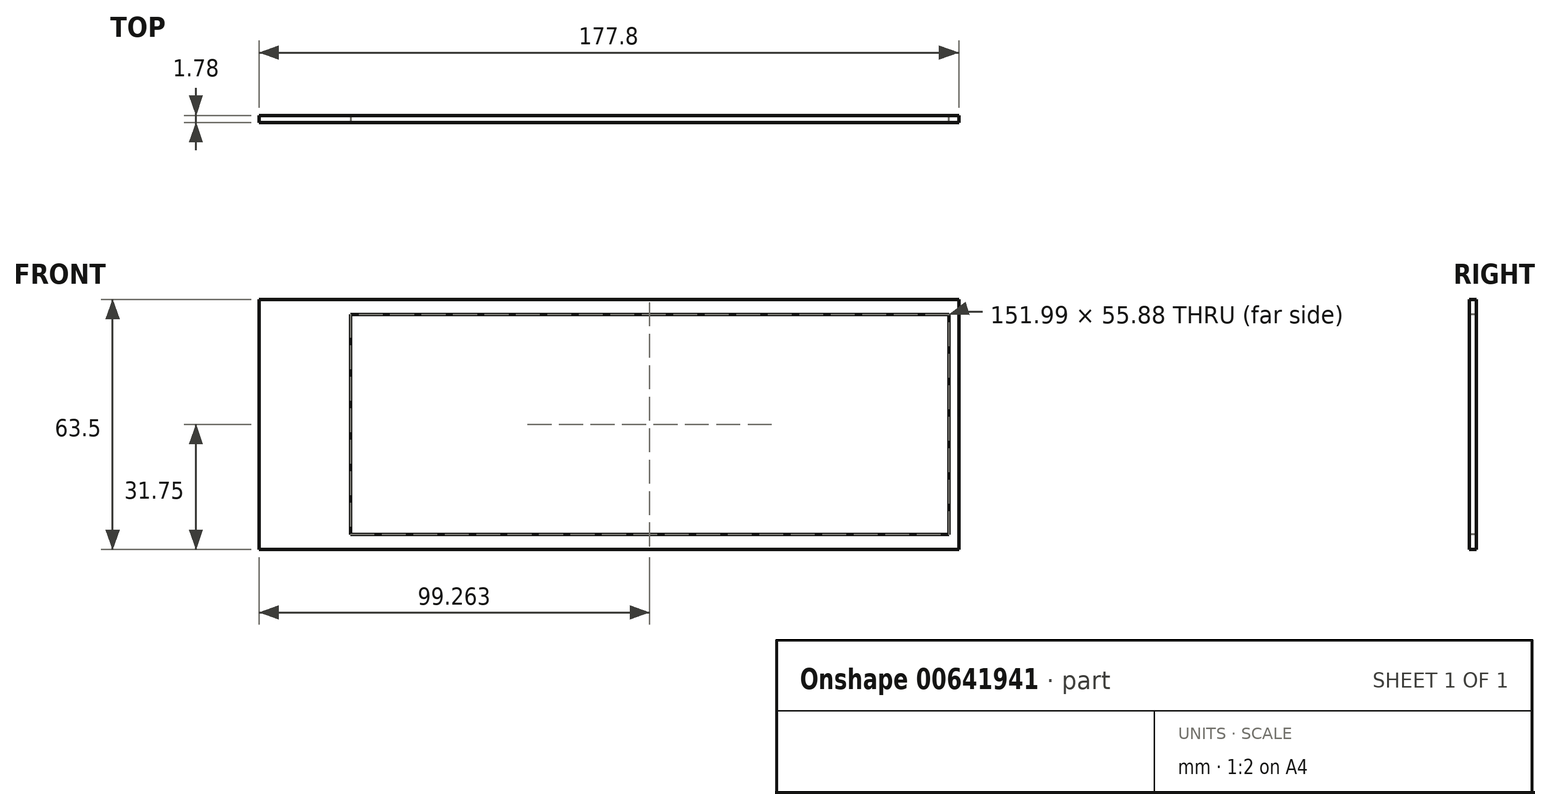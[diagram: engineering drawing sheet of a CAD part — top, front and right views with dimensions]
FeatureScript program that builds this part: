
annotation { "Feature Type Name" : "Feature", "Feature Type Description" : "" }
export const myFeature = defineFeature(function(context is Context, id is Id, definition is map)
    precondition{}
    {
        {
            var Q0;
            Q0=qCreatedBy(makeId("Front.planeOp"),FACE);
            var sketch = newSketch(context, id + "F0", { "sketchPlane" : qUnion([Q0])});
            skLineSegment(sketch, "E0.bottom", {"start": v(88.9, -31.75) * mm, "end": v(-88.9, -31.75) * mm});
            skLineSegment(sketch, "E0.top", {"start": v(88.9, 31.75) * mm, "end": v(-88.9, 31.75) * mm});
            skLineSegment(sketch, "E0.left", {"start": v(88.9, -31.75) * mm, "end": v(88.9, 31.75) * mm});
            skLineSegment(sketch, "E0.right", {"start": v(-88.9, -31.75) * mm, "end": v(-88.9, 31.75) * mm});
            skPoint(sketch, "E0.middle", {"position": v(0, 0) * mm});
            skLineSegment(sketch, "E1.bottom", {"start": v(86.36, -27.94) * mm, "end": v(-86.36, -27.94) * mm});
            skLineSegment(sketch, "E1.top", {"start": v(86.36, 27.94) * mm, "end": v(-86.36, 27.94) * mm});
            skLineSegment(sketch, "E1.left", {"start": v(86.36, -27.94) * mm, "end": v(86.36, 27.94) * mm});
            skLineSegment(sketch, "E1.right", {"start": v(-86.36, -27.94) * mm, "end": v(-86.36, 27.94) * mm});
            skLineSegment(sketch, "E2.bottom", {"start": v(-79.45, 27.94) * mm, "end": v(-72.54, 27.94) * mm});
            skLineSegment(sketch, "E2.top", {"start": v(-79.45, -27.94) * mm, "end": v(-72.54, -27.94) * mm});
            skLineSegment(sketch, "E2.left", {"start": v(-79.45, 27.94) * mm, "end": v(-79.45, -27.94) * mm});
            skLineSegment(sketch, "E2.right", {"start": v(-72.54, 27.94) * mm, "end": v(-72.54, -27.94) * mm});
            skLineSegment(sketch, "E3.1.0.0", {"start": v(-65.63, 27.94) * mm, "end": v(-58.72, 27.94) * mm});
            skLineSegment(sketch, "E3.1.0.1", {"start": v(-65.63, -27.94) * mm, "end": v(-58.72, -27.94) * mm});
            skLineSegment(sketch, "E3.1.0.2", {"start": v(-65.63, 27.94) * mm, "end": v(-65.63, -27.94) * mm});
            skLineSegment(sketch, "E3.1.0.3", {"start": v(-58.72, 27.94) * mm, "end": v(-58.72, -27.94) * mm});
            skLineSegment(sketch, "E3.2.0.0", {"start": v(-51.82, 27.94) * mm, "end": v(-44.9, 27.94) * mm});
            skLineSegment(sketch, "E3.2.0.1", {"start": v(-51.82, -27.94) * mm, "end": v(-44.9, -27.94) * mm});
            skLineSegment(sketch, "E3.2.0.2", {"start": v(-51.82, 27.94) * mm, "end": v(-51.82, -27.94) * mm});
            skLineSegment(sketch, "E3.2.0.3", {"start": v(-44.9, 27.94) * mm, "end": v(-44.9, -27.94) * mm});
            skLineSegment(sketch, "E3.direction1", {"start": v(-79.45, -27.94) * mm, "end": v(-65.63, -27.94) * mm, "construction": true});
            skLineSegment(sketch, "E4.0.3.0", {"start": v(-38, 27.94) * mm, "end": v(-31.09, 27.94) * mm});
            skLineSegment(sketch, "E4.3.3.0", {"start": v(-38, -27.94) * mm, "end": v(-31.09, -27.94) * mm});
            skLineSegment(sketch, "E4.6.3.0", {"start": v(-38, 27.94) * mm, "end": v(-38, -27.94) * mm});
            skLineSegment(sketch, "E4.9.3.0", {"start": v(-31.09, 27.94) * mm, "end": v(-31.09, -27.94) * mm});
            skLineSegment(sketch, "E4.0.4.0", {"start": v(-24.18, 27.94) * mm, "end": v(-17.27, 27.94) * mm});
            skLineSegment(sketch, "E4.3.4.0", {"start": v(-24.18, -27.94) * mm, "end": v(-17.27, -27.94) * mm});
            skLineSegment(sketch, "E4.6.4.0", {"start": v(-24.18, 27.94) * mm, "end": v(-24.18, -27.94) * mm});
            skLineSegment(sketch, "E4.9.4.0", {"start": v(-17.27, 27.94) * mm, "end": v(-17.27, -27.94) * mm});
            skLineSegment(sketch, "E4.0.5.0", {"start": v(-10.36, 27.94) * mm, "end": v(-3.45, 27.94) * mm});
            skLineSegment(sketch, "E4.3.5.0", {"start": v(-10.36, -27.94) * mm, "end": v(-3.45, -27.94) * mm});
            skLineSegment(sketch, "E4.6.5.0", {"start": v(-10.36, 27.94) * mm, "end": v(-10.36, -27.94) * mm});
            skLineSegment(sketch, "E4.9.5.0", {"start": v(-3.45, 27.94) * mm, "end": v(-3.45, -27.94) * mm});
            skLineSegment(sketch, "E4.0.6.0", {"start": v(3.45, 27.94) * mm, "end": v(10.36, 27.94) * mm});
            skLineSegment(sketch, "E4.3.6.0", {"start": v(3.45, -27.94) * mm, "end": v(10.36, -27.94) * mm});
            skLineSegment(sketch, "E4.6.6.0", {"start": v(3.45, 27.94) * mm, "end": v(3.45, -27.94) * mm});
            skLineSegment(sketch, "E4.9.6.0", {"start": v(10.36, 27.94) * mm, "end": v(10.36, -27.94) * mm});
            skLineSegment(sketch, "E4.0.7.0", {"start": v(17.27, 27.94) * mm, "end": v(24.18, 27.94) * mm});
            skLineSegment(sketch, "E4.3.7.0", {"start": v(17.27, -27.94) * mm, "end": v(24.18, -27.94) * mm});
            skLineSegment(sketch, "E4.6.7.0", {"start": v(17.27, 27.94) * mm, "end": v(17.27, -27.94) * mm});
            skLineSegment(sketch, "E4.9.7.0", {"start": v(24.18, 27.94) * mm, "end": v(24.18, -27.94) * mm});
            skLineSegment(sketch, "E4.0.8.0", {"start": v(31.09, 27.94) * mm, "end": v(38, 27.94) * mm});
            skLineSegment(sketch, "E4.3.8.0", {"start": v(31.09, -27.94) * mm, "end": v(38, -27.94) * mm});
            skLineSegment(sketch, "E4.6.8.0", {"start": v(31.09, 27.94) * mm, "end": v(31.09, -27.94) * mm});
            skLineSegment(sketch, "E4.9.8.0", {"start": v(38, 27.94) * mm, "end": v(38, -27.94) * mm});
            skLineSegment(sketch, "E4.0.9.0", {"start": v(44.9, 27.94) * mm, "end": v(51.82, 27.94) * mm});
            skLineSegment(sketch, "E4.3.9.0", {"start": v(44.9, -27.94) * mm, "end": v(51.82, -27.94) * mm});
            skLineSegment(sketch, "E4.6.9.0", {"start": v(44.9, 27.94) * mm, "end": v(44.9, -27.94) * mm});
            skLineSegment(sketch, "E4.9.9.0", {"start": v(51.82, 27.94) * mm, "end": v(51.82, -27.94) * mm});
            skLineSegment(sketch, "E4.0.10.0", {"start": v(58.72, 27.94) * mm, "end": v(65.63, 27.94) * mm});
            skLineSegment(sketch, "E4.3.10.0", {"start": v(58.72, -27.94) * mm, "end": v(65.63, -27.94) * mm});
            skLineSegment(sketch, "E4.6.10.0", {"start": v(58.72, 27.94) * mm, "end": v(58.72, -27.94) * mm});
            skLineSegment(sketch, "E4.9.10.0", {"start": v(65.63, 27.94) * mm, "end": v(65.63, -27.94) * mm});
            skLineSegment(sketch, "E4.0.11.0", {"start": v(72.54, 27.94) * mm, "end": v(79.45, 27.94) * mm});
            skLineSegment(sketch, "E4.3.11.0", {"start": v(72.54, -27.94) * mm, "end": v(79.45, -27.94) * mm});
            skLineSegment(sketch, "E4.6.11.0", {"start": v(72.54, 27.94) * mm, "end": v(72.54, -27.94) * mm});
            skLineSegment(sketch, "E4.9.11.0", {"start": v(79.45, 27.94) * mm, "end": v(79.45, -27.94) * mm});
            skSolve(sketch);
        }
        {
            var Q0;
            Q0=qSketchRegion(id+"F0",true);
            var Q1;
            Q1=makeQuery(id+"F0.imprint","IMPRINT",FACE,{"disambiguationData":[TD([[makeQuery(id+"F0.imprint","IMPRINT",EDGE,{"derivedFrom":sQuery(id+"F0.wireOp",EDGE,"E2.bottom")}),-1.0]])]});
            var Q2;
            Q2=makeQuery(id+"F0.imprint","IMPRINT",FACE,{"disambiguationData":[TD([[makeQuery(id+"F0.imprint","IMPRINT",EDGE,{"derivedFrom":sQuery(id+"F0.wireOp",EDGE,"E3.1.0.0")}),-1.0]])]});
            var Q3;
            Q3=makeQuery(id+"F0.imprint","IMPRINT",FACE,{"disambiguationData":[TD([[makeQuery(id+"F0.imprint","IMPRINT",EDGE,{"derivedFrom":sQuery(id+"F0.wireOp",EDGE,"E3.2.0.0")}),-1.0]])]});
            var Q4;
            Q4=makeQuery(id+"F0.imprint","IMPRINT",FACE,{"disambiguationData":[TD([[makeQuery(id+"F0.imprint","IMPRINT",EDGE,{"derivedFrom":sQuery(id+"F0.wireOp",EDGE,"E4.0.3.0")}),-1.0]])]});
            var Q5;
            Q5=makeQuery(id+"F0.imprint","IMPRINT",FACE,{"disambiguationData":[TD([[makeQuery(id+"F0.imprint","IMPRINT",EDGE,{"derivedFrom":sQuery(id+"F0.wireOp",EDGE,"E4.0.4.0")}),-1.0]])]});
            var Q6;
            Q6=makeQuery(id+"F0.imprint","IMPRINT",FACE,{"disambiguationData":[TD([[makeQuery(id+"F0.imprint","IMPRINT",EDGE,{"derivedFrom":sQuery(id+"F0.wireOp",EDGE,"E4.0.5.0")}),-1.0]])]});
            var Q7;
            Q7=makeQuery(id+"F0.imprint","IMPRINT",FACE,{"disambiguationData":[TD([[makeQuery(id+"F0.imprint","IMPRINT",EDGE,{"derivedFrom":sQuery(id+"F0.wireOp",EDGE,"E4.0.6.0")}),-1.0]])]});
            var Q8;
            Q8=makeQuery(id+"F0.imprint","IMPRINT",FACE,{"disambiguationData":[TD([[makeQuery(id+"F0.imprint","IMPRINT",EDGE,{"derivedFrom":sQuery(id+"F0.wireOp",EDGE,"E4.0.7.0")}),-1.0]])]});
            var Q9;
            Q9=makeQuery(id+"F0.imprint","IMPRINT",FACE,{"disambiguationData":[TD([[makeQuery(id+"F0.imprint","IMPRINT",EDGE,{"derivedFrom":sQuery(id+"F0.wireOp",EDGE,"E4.0.8.0")}),-1.0]])]});
            var Q10;
            Q10=makeQuery(id+"F0.imprint","IMPRINT",FACE,{"disambiguationData":[TD([[makeQuery(id+"F0.imprint","IMPRINT",EDGE,{"derivedFrom":sQuery(id+"F0.wireOp",EDGE,"E4.0.9.0")}),-1.0]])]});
            var Q11;
            Q11=makeQuery(id+"F0.imprint","IMPRINT",FACE,{"disambiguationData":[TD([[makeQuery(id+"F0.imprint","IMPRINT",EDGE,{"derivedFrom":sQuery(id+"F0.wireOp",EDGE,"E4.0.10.0")}),-1.0]])]});
            var Q12;
            Q12=makeQuery(id+"F0.imprint","IMPRINT",FACE,{"disambiguationData":[TD([[makeQuery(id+"F0.imprint","IMPRINT",EDGE,{"derivedFrom":sQuery(id+"F0.wireOp",EDGE,"E4.0.11.0")}),-1.0]])]});
            extrude(context, id + "F1", {"entities" : qUnion([Q0, Q1, Q2, Q3, Q4, Q5, Q6, Q7, Q8, Q9, Q10, Q11, Q12]), "depth" : 1.78 * mm});
        }
        {
            var Q0;
            Q0=makeQuery(id+"F1.opExtrude","CAP_FACE",FACE,{"disambiguationData":[OSD([sQuery(id+"F0.wireOp",EDGE,"E0.bottom"),sQuery(id+"F0.wireOp",EDGE,"E0.top"),sQuery(id+"F0.wireOp",EDGE,"E0.left"),sQuery(id+"F0.wireOp",EDGE,"E0.right"),sQuery(id+"F0.wireOp",EDGE,"E1.bottom"),sQuery(id+"F0.wireOp",EDGE,"E1.top"),sQuery(id+"F0.wireOp",EDGE,"E1.left"),sQuery(id+"F0.wireOp",EDGE,"E1.right"),sQuery(id+"F0.wireOp",EDGE,"E2.left"),sQuery(id+"F0.wireOp",EDGE,"E2.right"),sQuery(id+"F0.wireOp",EDGE,"E3.1.0.2"),sQuery(id+"F0.wireOp",EDGE,"E3.1.0.3"),sQuery(id+"F0.wireOp",EDGE,"E3.2.0.2"),sQuery(id+"F0.wireOp",EDGE,"E3.2.0.3"),sQuery(id+"F0.wireOp",EDGE,"E4.6.3.0"),sQuery(id+"F0.wireOp",EDGE,"E4.9.3.0"),sQuery(id+"F0.wireOp",EDGE,"E4.6.4.0"),sQuery(id+"F0.wireOp",EDGE,"E4.9.4.0"),sQuery(id+"F0.wireOp",EDGE,"E4.6.5.0"),sQuery(id+"F0.wireOp",EDGE,"E4.9.5.0"),sQuery(id+"F0.wireOp",EDGE,"E4.6.6.0"),sQuery(id+"F0.wireOp",EDGE,"E4.9.6.0"),sQuery(id+"F0.wireOp",EDGE,"E4.6.7.0"),sQuery(id+"F0.wireOp",EDGE,"E4.9.7.0"),sQuery(id+"F0.wireOp",EDGE,"E4.6.8.0"),sQuery(id+"F0.wireOp",EDGE,"E4.9.8.0"),sQuery(id+"F0.wireOp",EDGE,"E4.6.9.0"),sQuery(id+"F0.wireOp",EDGE,"E4.9.9.0"),sQuery(id+"F0.wireOp",EDGE,"E4.6.10.0"),sQuery(id+"F0.wireOp",EDGE,"E4.9.10.0"),sQuery(id+"F0.wireOp",EDGE,"E4.6.11.0"),sQuery(id+"F0.wireOp",EDGE,"E4.9.11.0")])],"isStart":false});
            var sketch = newSketch(context, id + "F2", { "sketchPlane" : qUnion([Q0])});
            skLineSegment(sketch, "E5.bottom", {"start": v(-86.36, 27.94) * mm, "end": v(-65.63, 27.94) * mm});
            skLineSegment(sketch, "E5.top", {"start": v(-86.36, -27.94) * mm, "end": v(-65.63, -27.94) * mm});
            skLineSegment(sketch, "E5.left", {"start": v(-86.36, 27.94) * mm, "end": v(-86.36, -27.94) * mm});
            skLineSegment(sketch, "E5.right", {"start": v(-65.63, 27.94) * mm, "end": v(-65.63, -27.94) * mm});
            skSolve(sketch);
        }
        {
            var Q0;
            Q0=qSketchRegion(id+"F2",true);
            extrude(context, id + "F3", {"entities" : qUnion([Q0]), "operationType" : NewBodyOperationType.ADD, "oppositeDirection" : true, "depth" : 1.78 * mm});
        }
    });
